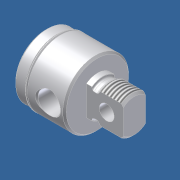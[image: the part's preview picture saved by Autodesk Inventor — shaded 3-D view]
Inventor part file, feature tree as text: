
AUTODESK INVENTOR PART (.ipt)
format: ipt  version: 2012 (Build 160160000, 160)  size: 258,048 bytes
history: native  units: in
note: dims shown in document units (in); Inventor stores cm internally (conversion verified against a paired STEP export)
features: other x155, sketch x7, revolve x5, extrude x2, thread x1
ambient origin geometry x8: Origin, YZ Plane, XZ Plane, XY Plane, X Axis, Y Axis, Z Axis, Center Point
bodies: Solid1 (feature_tree)
feature tree (170):
  other  "09P0010_rear_head"
  revolve  "Revolution1"  Angle=360.0deg
  revolve  "Revolution2"  [1 undecoded]
  thread  "Thread1"  [1 undecoded]
  extrude  "Extrusion1"  TaperAngle=360.0deg  [1 undecoded]
  revolve  "Revolution3"  [1 undecoded]
  revolve  "Revolution4"  [1 undecoded]
  revolve  "Revolution5"  [1 undecoded]
  extrude  "Extrusion2"  [1 undecoded]
  other  "c1_XY"
  other  "c1_YZ"
  other  "c1_ZX"
  other  "c1_X"
  other  "c1_Y"
  other  "c1_Z"
  other  "c1_Center"
  other  "cc1_XY"
  other  "cc1_YZ"
  other  "cc1_ZX"
  other  "cc1_X"
  other  "cc1_Y"
  other  "cc1_Z"
  other  "cc1_Center"
  other  "c2_XY"
  other  "c2_YZ"
  other  "c2_ZX"
  other  "c2_X"
  other  "c2_Y"
  other  "c2_Z"
  other  "c2_Center"
  other  "cc2_XY"
  other  "cc2_YZ"
  other  "cc2_ZX"
  other  "cc2_X"
  other  "cc2_Y"
  other  "cc2_Z"
  other  "cc2_Center"
  other  "to_tube_XY"
  other  "to_tube_YZ"
  other  "to_tube_ZX"
  other  "to_tube_X"
  other  "to_tube_Y"
  other  "to_tube_Z"
  other  "to_tube_Center"
  other  "to_nut_XY"
  other  "to_nut_YZ"
  other  "to_nut_ZX"
  other  "to_nut_X"
  other  "to_nut_Y"
  other  "to_nut_Z"
  other  "to_nut_Center"
  other  "lovra1_XY"
  other  "lovra1_YZ"
  other  "lovra1_ZX"
  other  "lovra1_X"
  other  "lovra1_Y"
  other  "lovra1_Z"
  other  "lovra1_Center"
  other  "lovra2_XY"
  other  "lovra2_YZ"
  other  "lovra2_ZX"
  other  "lovra2_X"
  other  "lovra2_Y"
  other  "lovra2_Z"
  other  "lovra2_Center"
  other  "lovra3_XY"
  other  "lovra3_YZ"
  other  "lovra3_ZX"
  other  "lovra3_X"
  other  "lovra3_Y"
  other  "lovra3_Z"
  other  "lovra3_Center"
  other  "to_pin_XY"
  other  "to_pin_YZ"
  other  "to_pin_ZX"
  other  "to_pin_X"
  other  "to_pin_Y"
  other  "to_pin_Z"
  other  "to_pin_Center"
  other  "olen_XY"
  other  "olen_YZ"
  other  "olen_ZX"
  other  "olen_X"
  other  "olen_Y"
  other  "olen_Z"
  other  "olen_Center"
  other  "thd1_XY"
  other  "thd1_YZ"
  other  "thd1_ZX"
  other  "thd1_X"
  other  "thd1_Y"
  other  "thd1_Z"
  other  "thd1_Center"
  other  "p1_XY"
  other  "p1_YZ"
  other  "p1_ZX"
  other  "p1_X"
  other  "p1_Y"
  other  "p1_Z"
  other  "p1_Center"
  other  "thd2_XY"
  other  "thd2_YZ"
  other  "thd2_ZX"
  other  "thd2_X"
  other  "thd2_Y"
  other  "thd2_Z"
  other  "thd2_Center"
  other  "p2_XY"
  other  "p2_YZ"
  other  "p2_ZX"
  other  "p2_X"
  other  "p2_Y"
  other  "p2_Z"
  other  "p2_Center"
  other  "port2_XY"
  other  "port2_YZ"
  other  "port2_ZX"
  other  "port2_X"
  other  "port2_Y"
  other  "port2_Z"
  other  "port2_Center"
  other  "port_XY"
  other  "port_YZ"
  other  "port_ZX"
  other  "port_X"
  other  "port_Y"
  other  "port_Z"
  other  "port_Center"
  other  "1_XY"
  other  "1_YZ"
  other  "1_ZX"
  other  "1_X"
  other  "1_Y"
  other  "1_Z"
  other  "1_Center"
  other  "lovra21_XY"
  other  "lovra21_YZ"
  other  "lovra21_ZX"
  other  "lovra21_X"
  other  "lovra21_Y"
  other  "lovra21_Z"
  other  "lovra21_Center"
  other  "lovra22_XY"
  other  "lovra22_YZ"
  other  "lovra22_ZX"
  other  "lovra22_X"
  other  "lovra22_Y"
  other  "lovra22_Z"
  other  "lovra22_Center"
  other  "to_screw_XY"
  other  "to_screw_YZ"
  other  "to_screw_ZX"
  other  "to_screw_X"
  other  "to_screw_Y"
  other  "to_screw_Z"
  other  "to_screw_Center"
  other  "to_mounting_bracket_XY"
  other  "to_mounting_bracket_YZ"
  other  "to_mounting_bracket_ZX"
  other  "to_mounting_bracket_X"
  other  "to_mounting_bracket_Y"
  other  "to_mounting_bracket_Z"
  other  "to_mounting_bracket_Center"
  sketch  "Sketch_18"  dims[d9=0.5587in d10=0.0in]
  sketch  "Sketch_15"  dims[d7=360.0deg d8=360.0deg]
  sketch  "Sketch_9"  dims[d0=360.0deg d1=360.0deg]
  sketch  "Sketch_13"  dims[d2=0.4208in d3=0.0in d4=0.625in d5=0.0in d6=360.0deg]
  sketch  "Sketch_19"
  sketch  "Sketch_24"
  sketch  "Sketch_43"
note: 7 required parameter values undecoded (feature->parameter linkage not recoverable at this tier; creation-order binding heuristic only, values carry confidence <= 0.55)